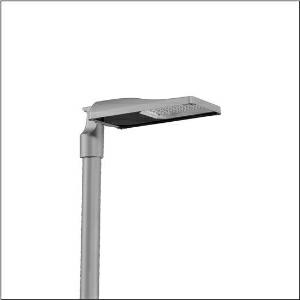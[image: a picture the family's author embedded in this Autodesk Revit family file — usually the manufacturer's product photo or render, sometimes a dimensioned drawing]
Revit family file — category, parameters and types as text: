
# Revit family: streetlight_sl_31_mini___st1_0a_5xh6d3ab08ga_4fba
name_source: partatom
category: Lighting Fixtures
units: mm (PartAtom-declared; Revit-internal decimal feet)

## family parameters
Cut with Voids When Loaded = No
Host = Face
Light Source = No
Part Type = Normal
Room Calculation Point = No
Round Connector Dimension = Use Diameter
Shared = No

## types (1)
- --- (1 x LED, 5710 lm, 37.3 W, 3000K)
    Apparent Load = 37 VA
    CIE Flux Codes = 37 72 97 100 100
    Color Rendering = 70
    Color Temperature = 3000K
    Default Elevation = 1800 mm
    Description = Streetlight SL 31 mini Easy LST mast luminaire for post-top, side-entry; light control with lens of PMMA; light distribution: ST1.0a, direct asymmetric distribution, for standard-compliant lighting for roads and squares; LED: luminous flux: 5.710lm, light colour: 730, colour temperature: 3000K; luminous efficacy: 153,1lm/W; control: pre-setting: linear dimming characteristic, flexible luminous flux parameterisation, time-dependent luminous flux control, constant luminous flux control, power reduction, intelligent temperature release in ECG and LED module, overheat protection; luminaire housing, of diecast aluminium, Siteco® metallic grey (DB 702S), corrosivity category C5 high according to DIN EN ISO 12944; cover of toughened safety glass, transparent, opened without tools; mast flange of diecast aluminium, Siteco® metallic grey (DB 702S), spigot size: 76/60mm, mast flange included unmounted; with cable H07RN-F 3x 1.5mm², cable length: 6,5m, connection cable pre-assembled; mains connection: 220..240V, AC, 50/60Hz; power consumption (at start of service life): 37,3W / (at end of service life): 38,7W / (with reduced operation 50%): 17,5W; protection rating (complete): IP66; insulation class (complete): insulation class II (safety insulation); impact resistance: IK10; certification: CE, ENEC, ENEC+, VDE, UKCA; permissible operating ambient temperature for outdoor applications: -40..+50°C; packaging unit: 1 piece

Light Distribution: ST1.0a
    Height = 76 mm
    Lamp = 1 x LED
    Lamp Light Flux = 5710 lm
    Lamp Power = 37.3 W
    Lamp count = 1
    Length = 547 mm
    Luminous efficacy = 153 lm/W
    Manufacturer = Siteco
    ModVariant = No
    Model = 5XH6D3AB08GA
    Number of Poles = 1
    OnlyDefault = Yes
    Power Factor = 1
    Product Name = Streetlight SL 31 mini | ST1.0a
    Product group = mast luminaire | pylon top
    ProductGroupID = 6100
    Protection Class = Protection class II
    Protection Degree = IP 66
    RLX_Detail_Level = 1
    RLX_Emergency_Light_Flux = 0 lm
    RLX_Emergency_Type = 0
    RLX_Emergency_Type_DB = No
    RlxData = <blob elided: 39497 chars, md5=9ed36903>
    Socket = socket
    Standby Power = 0 W
    System Light Flux = 5710 lm
    System Power = 37 W
    Type Comments = factory setting: luminous flux: 100 % | dim-lin: 254 | 386 mA
    Type Image = l_1300326.jpg
    URL = http://relux.com
    VarID = @adj_054192
    Voltage = 0 V
    Weight = 0.00 kg
    Width = 265 mm

## geometry (parser evidence)
native form markers: Blend x4, Sweep x8
no freeform markers — native parametric forms only
